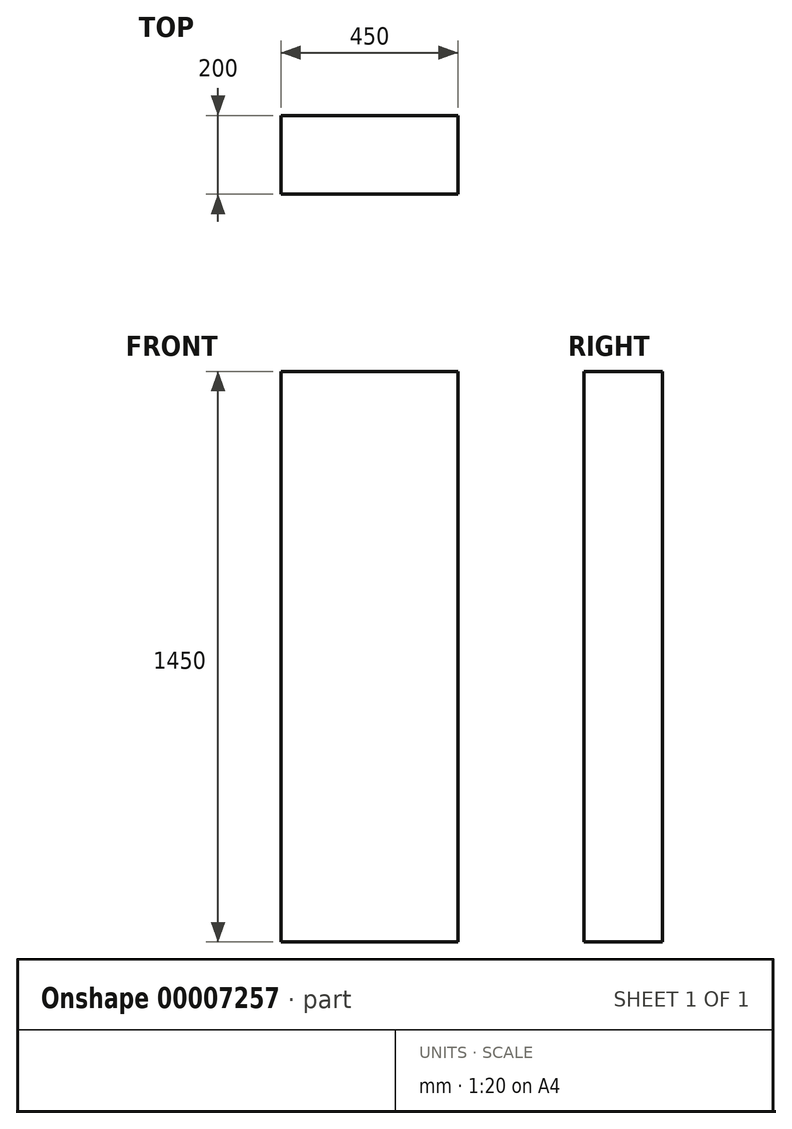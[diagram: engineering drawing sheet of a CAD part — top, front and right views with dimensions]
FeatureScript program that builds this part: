
annotation { "Feature Type Name" : "Feature", "Feature Type Description" : "" }
export const myFeature = defineFeature(function(context is Context, id is Id, definition is map)
    precondition{}
    {
        {
            var Q0;
            Q0=qCreatedBy(makeId("Front.planeOp"),FACE);
            var sketch = newSketch(context, id + "F0", { "sketchPlane" : qUnion([Q0])});
            skLineSegment(sketch, "E0.bottom", {"start": v(0, 0) * mm, "end": v(450, 0) * mm});
            skLineSegment(sketch, "E0.top", {"start": v(0, 1450) * mm, "end": v(450, 1450) * mm});
            skLineSegment(sketch, "E0.left", {"start": v(0, 0) * mm, "end": v(0, 1450) * mm});
            skLineSegment(sketch, "E0.right", {"start": v(450, 0) * mm, "end": v(450, 1450) * mm});
            skSolve(sketch);
        }
        {
            var Q0;
            Q0=makeQuery(id+"F0.imprint","IMPRINT",FACE,{"disambiguationData":[TD([[makeQuery(id+"F0.imprint","IMPRINT",EDGE,{"derivedFrom":sQuery(id+"F0.wireOp",EDGE,"E0.bottom")}),1.0]])]});
            extrude(context, id + "F1", {"entities" : qUnion([Q0]), "depth" : 200 * mm});
        }
    });
